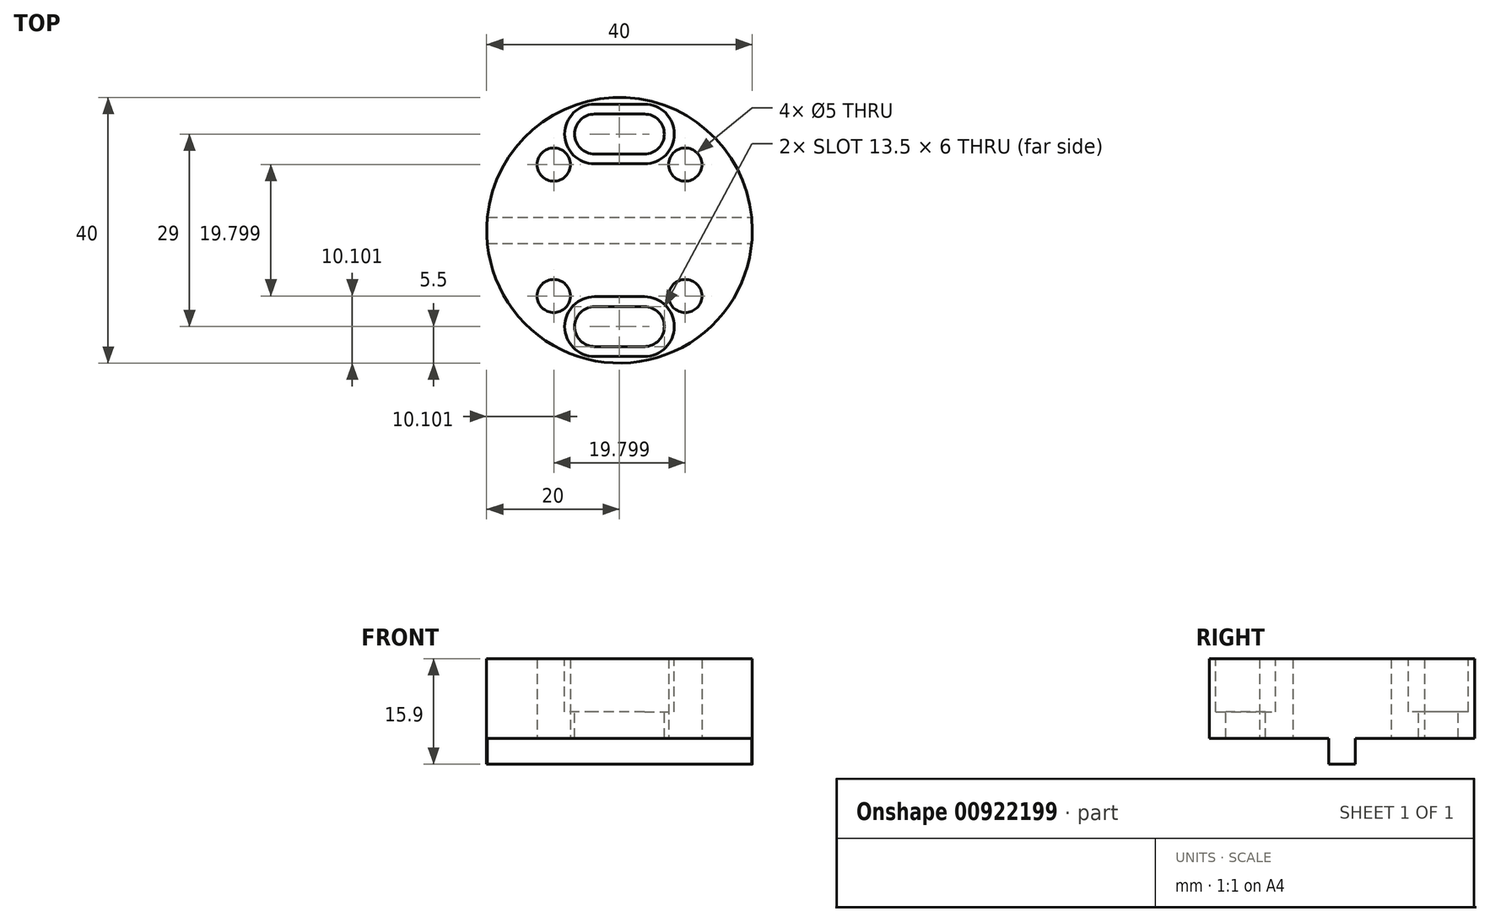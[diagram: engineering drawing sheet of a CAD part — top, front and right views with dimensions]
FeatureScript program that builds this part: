
annotation { "Feature Type Name" : "Feature", "Feature Type Description" : "" }
export const myFeature = defineFeature(function(context is Context, id is Id, definition is map)
    precondition{}
    {
        {
            var Q0;
            Q0=qCreatedBy(makeId("Top.planeOp"),FACE);
            var sketch = newSketch(context, id + "F0", { "sketchPlane" : qUnion([Q0])});
            skCircle(sketch, "E0", {"center": v(0, 0) * mm, "radius": 20 * mm});
            skCircle(sketch, "E1", {"center": v(0, 0) * mm, "radius": 14 * mm, "construction": true});
            skLineSegment(sketch, "E2", {"start": v(0, 0) * mm, "end": v(18.43, 18.43) * mm, "construction": true});
            skCircle(sketch, "E3", {"center": v(9.9, 9.9) * mm, "radius": 2.5 * mm});
            skCircle(sketch, "E4.1.0", {"center": v(-9.9, 9.9) * mm, "radius": 2.5 * mm});
            skCircle(sketch, "E4.2.0", {"center": v(-9.9, -9.9) * mm, "radius": 2.5 * mm});
            skCircle(sketch, "E4.3.0", {"center": v(9.9, -9.9) * mm, "radius": 2.5 * mm});
            skSolve(sketch);
        }
        {
            var Q0;
            Q0=makeQuery(id+"F0.imprint","IMPRINT",FACE,{"disambiguationData":[TD([[makeQuery(id+"F0.imprint","IMPRINT",EDGE,{"derivedFrom":sQuery(id+"F0.wireOp",EDGE,"E0")}),1.0]])]});
            extrude(context, id + "F1", {"entities" : qUnion([Q0]), "depth" : (12) * mm, "offsetDistance" : 25 * mm});
        }
        {
            var Q0;
            Q0=makeQuery(id+"F1.opExtrude","CAP_FACE",FACE,{"disambiguationData":[OSD([sQuery(id+"F0.wireOp",EDGE,"E0"),sQuery(id+"F0.wireOp",EDGE,"E3"),sQuery(id+"F0.wireOp",EDGE,"E4.1.0"),sQuery(id+"F0.wireOp",EDGE,"E4.2.0"),sQuery(id+"F0.wireOp",EDGE,"E4.3.0")])],"isStart":true});
            var sketch = newSketch(context, id + "F2", { "sketchPlane" : qUnion([Q0])});
            skLineSegment(sketch, "E5", {"start": v(-19.9, 1.98) * mm, "end": v(19.9, 1.98) * mm});
            skLineSegment(sketch, "E6", {"start": v(-19.9, -1.98) * mm, "end": v(19.9, -1.98) * mm});
            skSolve(sketch);
        }
        {
            var Q0;
            {var subQ0=sQuery(id+"F2.wireOp",EDGE,"E5");Q0=makeQuery(id+"F2.imprint","IMPRINT",FACE,{"disambiguationData":[TD([[makeQuery(id+"F2.imprint","IMPRINT",EDGE,{"derivedFrom":subQ0}),-1.0]])]});}
            extrude(context, id + "F3", {"entities" : qUnion([Q0]), "operationType" : NewBodyOperationType.ADD, "depth" : 3.9 * mm, "offsetDistance" : 25 * mm});
        }
        {
            var Q0;
            Q0=makeQuery(id+"F1.opExtrude","CAP_FACE",FACE,{"disambiguationData":[OSD([sQuery(id+"F0.wireOp",EDGE,"E0"),sQuery(id+"F0.wireOp",EDGE,"E3"),sQuery(id+"F0.wireOp",EDGE,"E4.1.0"),sQuery(id+"F0.wireOp",EDGE,"E4.2.0"),sQuery(id+"F0.wireOp",EDGE,"E4.3.0")])],"isStart":false});
            var sketch = newSketch(context, id + "F4", { "sketchPlane" : qUnion([Q0])});
            skLineSegment(sketch, "E7", {"start": v(-3.75, 17.5) * mm, "end": v(3.75, 17.5) * mm});
            skArc(sketch, "E8", {"start": v(3.75, 17.5) * mm, "mid": v(6.75, 14.5) * mm, "end": v(3.75, 11.5) * mm});
            skLineSegment(sketch, "E9", {"start": v(3.75, 11.5) * mm, "end": v(-3.75, 11.5) * mm});
            skArc(sketch, "E10", {"start": v(-3.75, 11.5) * mm, "mid": v(-6.75, 14.5) * mm, "end": v(-3.75, 17.5) * mm});
            skLineSegment(sketch, "E11", {"start": v(0, 25.86) * mm, "end": v(0, -24.36) * mm, "construction": true});
            skLineSegment(sketch, "E12.MirrorCS", {"start": v(3.75, -11.5) * mm, "end": v(-3.75, -11.5) * mm});
            skLineSegment(sketch, "E13.MirrorCS", {"start": v(-3.75, -17.5) * mm, "end": v(3.75, -17.5) * mm});
            skArc(sketch, "E14.MirrorCS", {"start": v(-3.75, -11.5) * mm, "mid": v(-6.75, -14.5) * mm, "end": v(-3.75, -17.5) * mm});
            skArc(sketch, "E15.MirrorCS", {"start": v(3.75, -17.5) * mm, "mid": v(6.75, -14.5) * mm, "end": v(3.75, -11.5) * mm});
            skSolve(sketch);
        }
        {
            var Q0;
            Q0=makeQuery(id+"F4.imprint","IMPRINT",FACE,{"disambiguationData":[TD([[makeQuery(id+"F4.imprint","IMPRINT",EDGE,{"derivedFrom":sQuery(id+"F4.wireOp",EDGE,"E7")}),-1.0]])]});
            var Q1;
            Q1=makeQuery(id+"F4.imprint","IMPRINT",FACE,{"disambiguationData":[TD([[makeQuery(id+"F4.imprint","IMPRINT",EDGE,{"derivedFrom":sQuery(id+"F4.wireOp",EDGE,"E12.MirrorCS")}),1.0]])]});
            extrude(context, id + "F5", {"entities" : qUnion([Q0, Q1]), "operationType" : NewBodyOperationType.REMOVE, "endBound" : BoundingType.THROUGH_ALL, "oppositeDirection" : true, "depth" : 25 * mm, "offsetDistance" : 25 * mm});
        }
        {
            var Q0;
            Q0=makeQuery(id+"F1.opExtrude","CAP_FACE",FACE,{"disambiguationData":[OSD([sQuery(id+"F0.wireOp",EDGE,"E0"),sQuery(id+"F0.wireOp",EDGE,"E3"),sQuery(id+"F0.wireOp",EDGE,"E4.1.0"),sQuery(id+"F0.wireOp",EDGE,"E4.2.0"),sQuery(id+"F0.wireOp",EDGE,"E4.3.0")])],"isStart":false});
            var sketch = newSketch(context, id + "F6", { "sketchPlane" : qUnion([Q0])});
            skLineSegment(sketch, "E16.0", {"start": v(-3.75, 19) * mm, "end": v(3.75, 19) * mm});
            skArc(sketch, "E16.1", {"start": v(-3.75, 10) * mm, "mid": v(-8.25, 14.5) * mm, "end": v(-3.75, 19) * mm});
            skLineSegment(sketch, "E16.2", {"start": v(3.75, 10) * mm, "end": v(-3.75, 10) * mm});
            skArc(sketch, "E16.3", {"start": v(3.75, 19) * mm, "mid": v(8.25, 14.5) * mm, "end": v(3.75, 10) * mm});
            skLineSegment(sketch, "E17.0", {"start": v(3.75, -10) * mm, "end": v(-3.75, -10) * mm});
            skArc(sketch, "E17.1", {"start": v(3.75, -19) * mm, "mid": v(8.25, -14.5) * mm, "end": v(3.75, -10) * mm});
            skLineSegment(sketch, "E17.2", {"start": v(-3.75, -19) * mm, "end": v(3.75, -19) * mm});
            skArc(sketch, "E17.3", {"start": v(-3.75, -10) * mm, "mid": v(-8.25, -14.5) * mm, "end": v(-3.75, -19) * mm});
            skSolve(sketch);
        }
        {
            var Q0;
            Q0=makeQuery(id+"F6.imprint","IMPRINT",FACE,{"disambiguationData":[TD([[makeQuery(id+"F6.imprint","IMPRINT",EDGE,{"derivedFrom":sQuery(id+"F6.wireOp",EDGE,"E16.0")}),-1.0]])]});
            var Q1;
            Q1=makeQuery(id+"F6.imprint","IMPRINT",FACE,{"disambiguationData":[TD([[makeQuery(id+"F6.imprint","IMPRINT",EDGE,{"derivedFrom":sQuery(id+"F6.wireOp",EDGE,"E17.0")}),1.0]])]});
            extrude(context, id + "F7", {"entities" : qUnion([Q0, Q1]), "operationType" : NewBodyOperationType.REMOVE, "oppositeDirection" : true, "depth" : (8) * mm, "offsetDistance" : 25 * mm});
        }
    });
